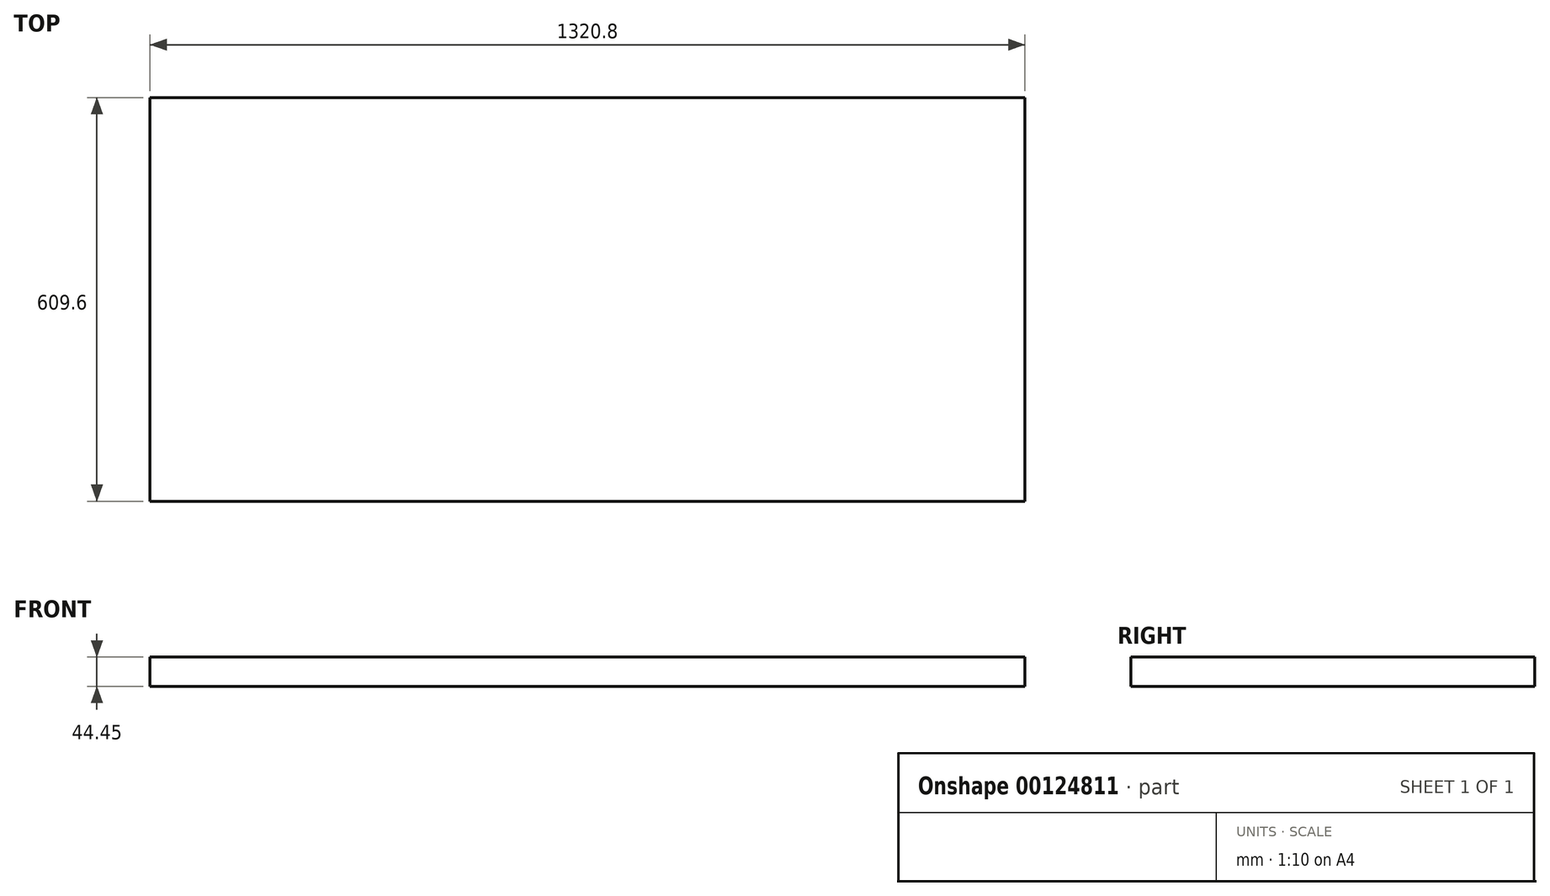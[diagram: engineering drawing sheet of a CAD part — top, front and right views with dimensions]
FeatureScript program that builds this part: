
annotation { "Feature Type Name" : "Feature", "Feature Type Description" : "" }
export const myFeature = defineFeature(function(context is Context, id is Id, definition is map)
    precondition{}
    {
        {
            var Q0;
            Q0=qCreatedBy(makeId("Top.planeOp"),FACE);
            var sketch = newSketch(context, id + "F0", { "sketchPlane" : qUnion([Q0])});
            skLineSegment(sketch, "E0.bottom", {"start": v(-660.4, 304.8) * mm, "end": v(660.4, 304.8) * mm});
            skLineSegment(sketch, "E0.top", {"start": v(-660.4, -304.8) * mm, "end": v(660.4, -304.8) * mm});
            skLineSegment(sketch, "E0.left", {"start": v(-660.4, 304.8) * mm, "end": v(-660.4, -304.8) * mm});
            skLineSegment(sketch, "E0.right", {"start": v(660.4, 304.8) * mm, "end": v(660.4, -304.8) * mm});
            skSolve(sketch);
        }
        {
            var Q0;
            Q0=makeQuery(id+"F0.imprint","IMPRINT",FACE,{"disambiguationData":[TD([[makeQuery(id+"F0.imprint","IMPRINT",EDGE,{"derivedFrom":sQuery(id+"F0.wireOp",EDGE,"E0.bottom")}),-1.0]])]});
            extrude(context, id + "F1", {"entities" : qUnion([Q0]), "depth" : 44.45 * mm});
        }
    });
